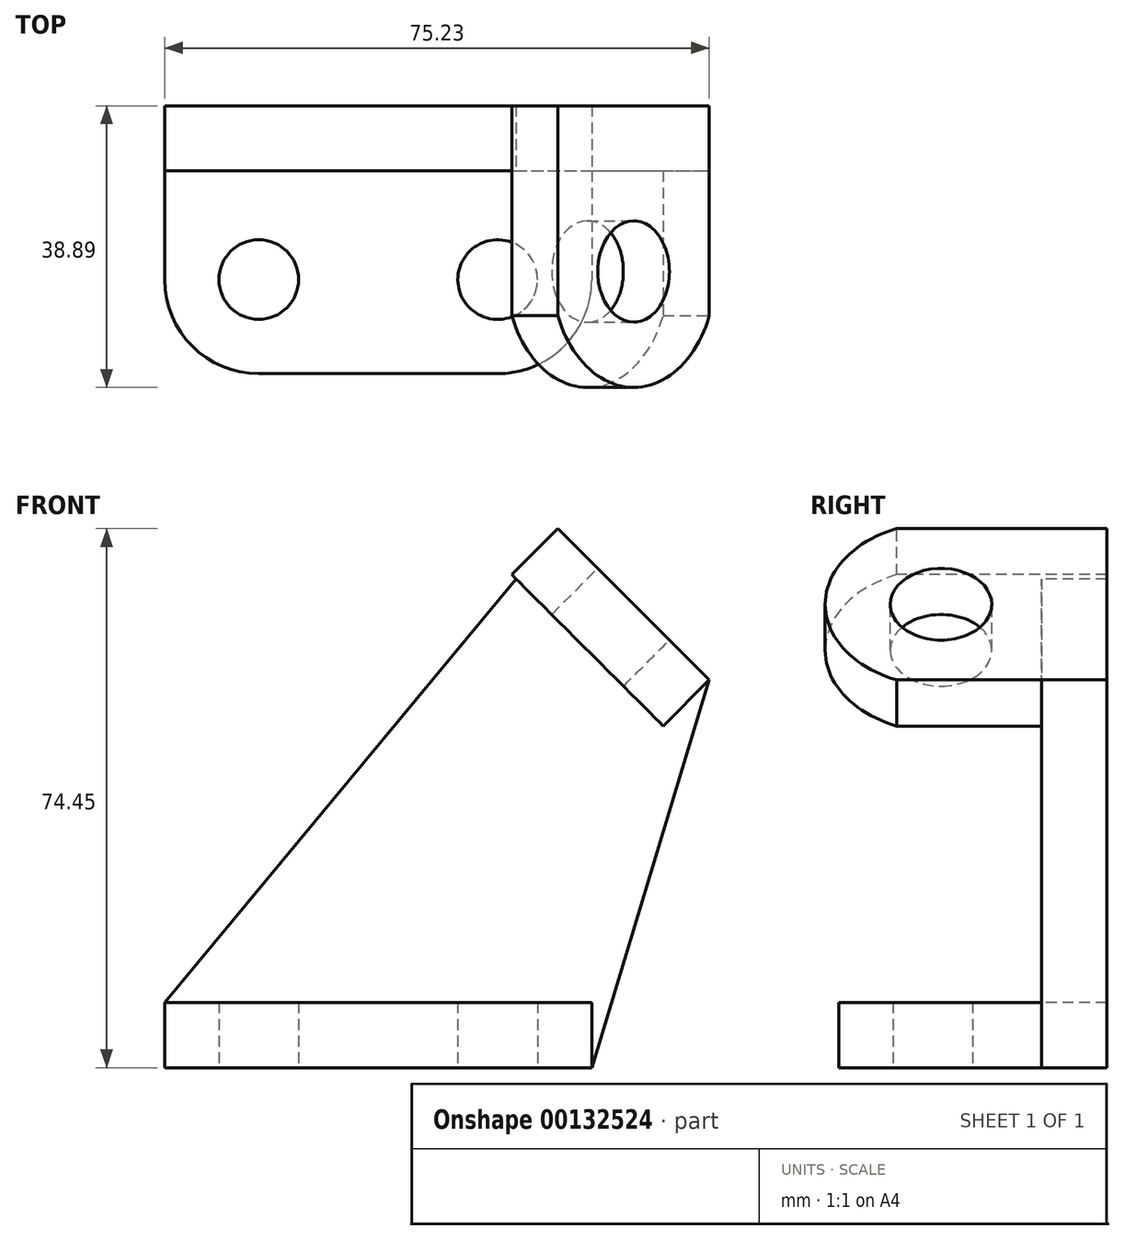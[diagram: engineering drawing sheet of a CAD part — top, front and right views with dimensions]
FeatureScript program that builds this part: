
annotation { "Feature Type Name" : "Feature", "Feature Type Description" : "" }
export const myFeature = defineFeature(function(context is Context, id is Id, definition is map)
    precondition{}
    {
        {
            var Q0;
            Q0=qCreatedBy(makeId("Top.planeOp"),FACE);
            var sketch = newSketch(context, id + "F0", { "sketchPlane" : qUnion([Q0])});
            skLineSegment(sketch, "E0", {"start": v(-13, 17.39) * mm, "end": v(46, 17.39) * mm});
            skLineSegment(sketch, "E1", {"start": v(46, 17.39) * mm, "end": v(46, 2.39) * mm});
            skLineSegment(sketch, "E2", {"start": v(-13, 17.39) * mm, "end": v(-13, 2.39) * mm});
            skArc(sketch, "E3", {"start": v(-13, 2.39) * mm, "mid": v(-9.2, -6.8) * mm, "end": v(0, -10.61) * mm});
            skArc(sketch, "E4", {"start": v(33, -10.61) * mm, "mid": v(42.2, -6.8) * mm, "end": v(46, 2.39) * mm});
            skLineSegment(sketch, "E5", {"start": v(0, -10.61) * mm, "end": v(33, -10.61) * mm});
            skCircle(sketch, "E6", {"center": v(0, 2.39) * mm, "radius": 5.5 * mm});
            skCircle(sketch, "E7", {"center": v(33, 2.39) * mm, "radius": 5.5 * mm});
            skSolve(sketch);
        }
        {
            var Q0;
            Q0 = qSketchRegion(id + "F0", true);
            extrude(context, id + "F1", {"entities" : qUnion([Q0]), "depth" : 9 * mm});
        }
        {
            var Q0;
            Q0=qCreatedBy(makeId("Front.planeOp"),FACE);
            var sketch = newSketch(context, id + "F2", { "sketchPlane" : qUnion([Q0])});
            skLineSegment(sketch, "E8.0", {"start": v(-13, 0) * mm, "end": v(46, 0) * mm});
            skLineSegment(sketch, "E9.0", {"start": v(-13, 9) * mm, "end": v(46, 9) * mm});
            skLineSegment(sketch, "E10", {"start": v(-13, 9) * mm, "end": v(41.32, 74.45) * mm});
            skLineSegment(sketch, "E11", {"start": v(46, 0) * mm, "end": v(62.23, 53.55) * mm});
            skLineSegment(sketch, "E12", {"start": v(62.23, 53.55) * mm, "end": v(41.32, 74.45) * mm});
            skLineSegment(sketch, "E13", {"start": v(-13, 0) * mm, "end": v(-13, 9) * mm});
            skLineSegment(sketch, "E14", {"start": v(51.77, 64) * mm, "end": v(83.03, 64) * mm, "construction": true});
            skLineSegment(sketch, "E15", {"start": v(46, 0) * mm, "end": v(46, 9) * mm});
            skSolve(sketch);
        }
        {
            var Q0;
            Q0 = qSketchRegion(id + "F2", true);
            var Q1;
            Q1=makeQuery(id+"F1.opExtrude","SWEPT_FACE",FACE,{"disambiguationData":[OSD([sQuery(id+"F0.wireOp",EDGE,"E0")])]});
            var Q2;
            Q2=makeQuery(id+"F1.opExtrude","SWEPT_FACE",FACE,{"disambiguationData":[OSD([sQuery(id+"F0.wireOp",EDGE,"E0")])]});
            extrude(context, id + "F3", {"entities" : qUnion([Q0]), "operationType" : NewBodyOperationType.ADD, "oppositeDirection" : true, "endBoundEntityFace" : qUnion([Q1]), "depth" : 26.4 * mm, "hasSecondDirection" : true, "secondDirectionBound" : SecondDirectionBoundingType.UP_TO_SURFACE, "secondDirectionOppositeDirection" : true, "secondDirectionBoundEntityFace" : qUnion([Q2]), "secondDirectionDepth" : 15.74 * mm});
        }
        {
            var Q0;
            Q0=makeQuery(id+"F3.opExtrude","SWEPT_FACE",FACE,{"disambiguationData":[OSD([sQuery(id+"F2.wireOp",EDGE,"E12")])]});
            cPlane(context, id + "F4", {"entities" : qUnion([Q0]), "cplaneType" : CPlaneType.OFFSET, "offset" : 0 * mm, "width" : 150 * mm, "height" : 150 * mm});
        }
        {
            var Q0;
            Q0=qCreatedBy(id+"F4.planeOp",FACE);
            var sketch = newSketch(context, id + "F5", { "sketchPlane" : qUnion([Q0])});
            skLineSegment(sketch, "E16.0", {"start": v(26.39, -6.14) * mm, "end": v(26.39, 23.43) * mm});
            skLineSegment(sketch, "E17", {"start": v(26.39, 23.43) * mm, "end": v(-2.61, 23.43) * mm});
            skLineSegment(sketch, "E18", {"start": v(26.39, -6.14) * mm, "end": v(-2.61, -6.14) * mm});
            skArc(sketch, "E19", {"start": v(-2.61, 23.43) * mm, "mid": v(-12.5, 8.65) * mm, "end": v(-2.61, -6.14) * mm});
            skCircle(sketch, "E20", {"center": v(3.5, 8.65) * mm, "radius": 7 * mm});
            skSolve(sketch);
        }
        {
            var Q0;
            Q0 = qSketchRegion(id + "F5", true);
            extrude(context, id + "F6", {"entities" : qUnion([Q0]), "operationType" : NewBodyOperationType.ADD, "oppositeDirection" : true, "depth" : 9 * mm});
        }
    });
